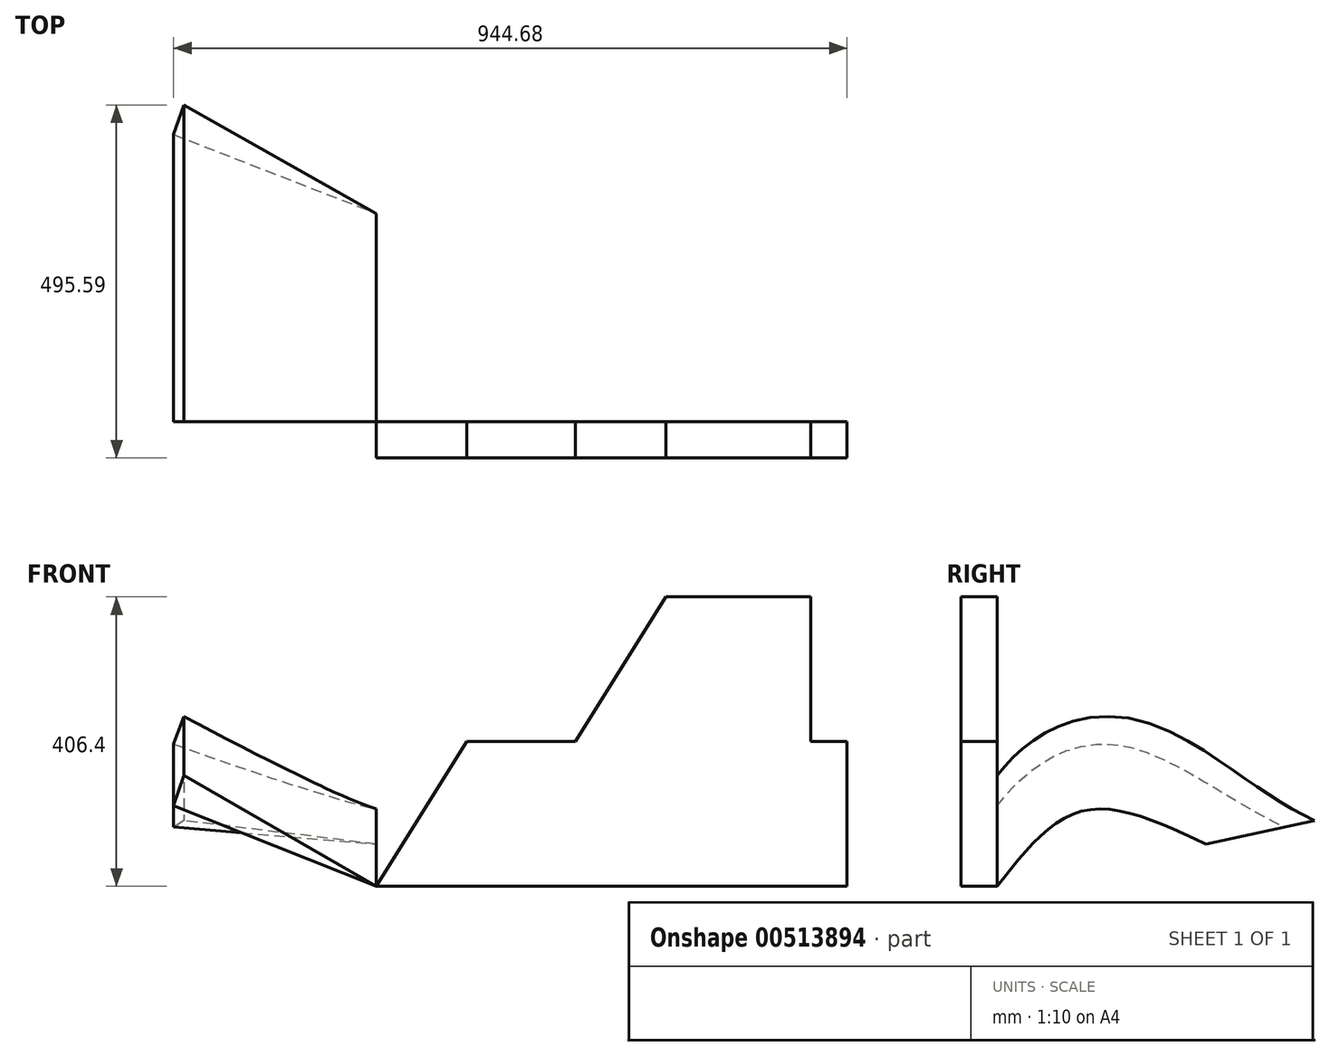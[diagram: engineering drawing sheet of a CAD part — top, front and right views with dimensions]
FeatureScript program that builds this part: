
annotation { "Feature Type Name" : "Feature", "Feature Type Description" : "" }
export const myFeature = defineFeature(function(context is Context, id is Id, definition is map)
    precondition{}
    {
        {
            var Q0;
            Q0=qCreatedBy(makeId("Front.planeOp"),FACE);
            var sketch = newSketch(context, id + "F0", { "sketchPlane" : qUnion([Q0])});
            skLineSegment(sketch, "E0", {"start": v(0, 0) * mm, "end": v(660.4, 0) * mm});
            skLineSegment(sketch, "E1", {"start": v(660.4, 0) * mm, "end": v(660.4, 203.2) * mm});
            skLineSegment(sketch, "E2", {"start": v(660.4, 203.2) * mm, "end": v(609.6, 203.2) * mm});
            skLineSegment(sketch, "E3", {"start": v(609.6, 203.2) * mm, "end": v(609.6, 406.4) * mm});
            skLineSegment(sketch, "E4", {"start": v(609.6, 406.4) * mm, "end": v(406.4, 406.4) * mm});
            skLineSegment(sketch, "E5", {"start": v(406.4, 406.4) * mm, "end": v(279.4, 203.2) * mm});
            skLineSegment(sketch, "E6", {"start": v(279.4, 203.2) * mm, "end": v(127, 203.2) * mm});
            skLineSegment(sketch, "E7", {"start": v(127, 203.2) * mm, "end": v(0, 0) * mm});
            skSolve(sketch);
        }
        {
            var Q0;
            Q0=makeQuery(id+"F0.imprint","IMPRINT",FACE,{"disambiguationData":[TD([[makeQuery(id+"F0.imprint","IMPRINT",EDGE,{"derivedFrom":sQuery(id+"F0.wireOp",EDGE,"E0")}),1.0]])]});
            extrude(context, id + "F1", {"entities" : qUnion([Q0]), "depth" : 50.8 * mm, "offsetDistance" : 25.4 * mm});
        }
        {
            var Q0;
            Q0=qCreatedBy(makeId("Front.planeOp"),FACE);
            var sketch = newSketch(context, id + "F2", { "sketchPlane" : qUnion([Q0])});
            skLineSegment(sketch, "E8", {"start": v(0, 0) * mm, "end": v(-270.07, 155.8) * mm});
            skLineSegment(sketch, "E9", {"start": v(-270.07, 155.8) * mm, "end": v(-284.28, 113.18) * mm});
            skLineSegment(sketch, "E10", {"start": v(-284.28, 113.18) * mm, "end": v(0, 0) * mm});
            skSolve(sketch);
        }
        {
            var Q0;
            Q0=qCreatedBy(makeId("Right.planeOp"),FACE);
            var sketch = newSketch(context, id + "F3", { "sketchPlane" : qUnion([Q0])});
            skFitSpline(sketch, "E11", {"points": [v(0, 0) * mm, v(120.8, 106) * mm, v(292.54, 59.25) * mm], "startDerivative": vector(226.73, 292.8) * mm, "endDerivative": vector(357.25, -170.36) * mm});
            skSolve(sketch);
        }
        {
            var Q0;
            Q0=makeQuery(id+"F2.imprint","IMPRINT",FACE,{"disambiguationData":[TD([[makeQuery(id+"F2.imprint","IMPRINT",EDGE,{"derivedFrom":sQuery(id+"F2.wireOp",EDGE,"E8")}),1.0]])]});
            var Q1;
            Q1=sQuery(id+"F3.wireOp",EDGE,"E11");
            sweep(context, id + "F4", {"profiles" : qUnion([Q0]), "path" : qUnion([Q1])});
        }
    });
